# Revit family: Plumbing-Flushometer-Sloan-Valve-ROYAL-111-ESS_
name_source: partatom
category: Plumbing Fixtures
units: mm (PartAtom-declared; Revit-internal decimal feet)

## family parameters
Cut with Voids When Loaded = No
Host = Face
Maintain Annotation Orientation = No
OmniClass Number = 23.45.05.14.99
OmniClass Title = Other Sanitary Washing Plumbing Fixtures
Part Type = Normal
Room Calculation Point = No
Round Connector Dimension = Use Diameter
Shared = No

## types (1)
- Not a Type - Load Type Catalog!
    Apparent Load = 0 VA
    Assembly Code = D2020300
    CW Connection = Yes
    CWFU = 0
    Centerline of Supply from Top of Fixture = 11 1/2"
    Centerline of Supply to Centerline of Valve = 4 3/4"
    Current = 0 A
    Date Updated = 09.12.2024
    Default Elevation = 0"
    Description = 1.28 gpf, Polished Chrome Finish, Fixture Connection Top Spud, Single Flush, True Mechanical Override, Sensor-Operated, Royal® Exposed Sensor Hardwired Water Closet Flushometer.
    Edition number = 1
    Flush Rate = 1.28 gpf (4.8 Lpf)
    HW Connection = No
    HWFU = 0
    Height = 13 5/8"
    Keynote = 15410
    Manufacturer = Sloan Valve
    Model = Model not specified - Load type catalog!
    Number of Poles = 3
    Operating Water Pressure = 15 – 80 PSI (103 – 552 kPa)
    Part Number = 3450055
    Power Factor = 0.8
    Product Material = Sloan Valve - Finish - Polished Chrome
    Product data url = https://bimobject.com
    URL = www.sloanvalve.com
    Valve Pressure Drop = 0.00 psi
    Vent Connection = No
    Version = 2
    Voltage = 24 V
    WFU = 0
    Waste Connection = No
    Water Inlet Connection Diameter = 1"
    z_Electrical Box = Yes

## geometry (parser evidence)
native form markers: Sweep x5
no freeform markers — native parametric forms only
